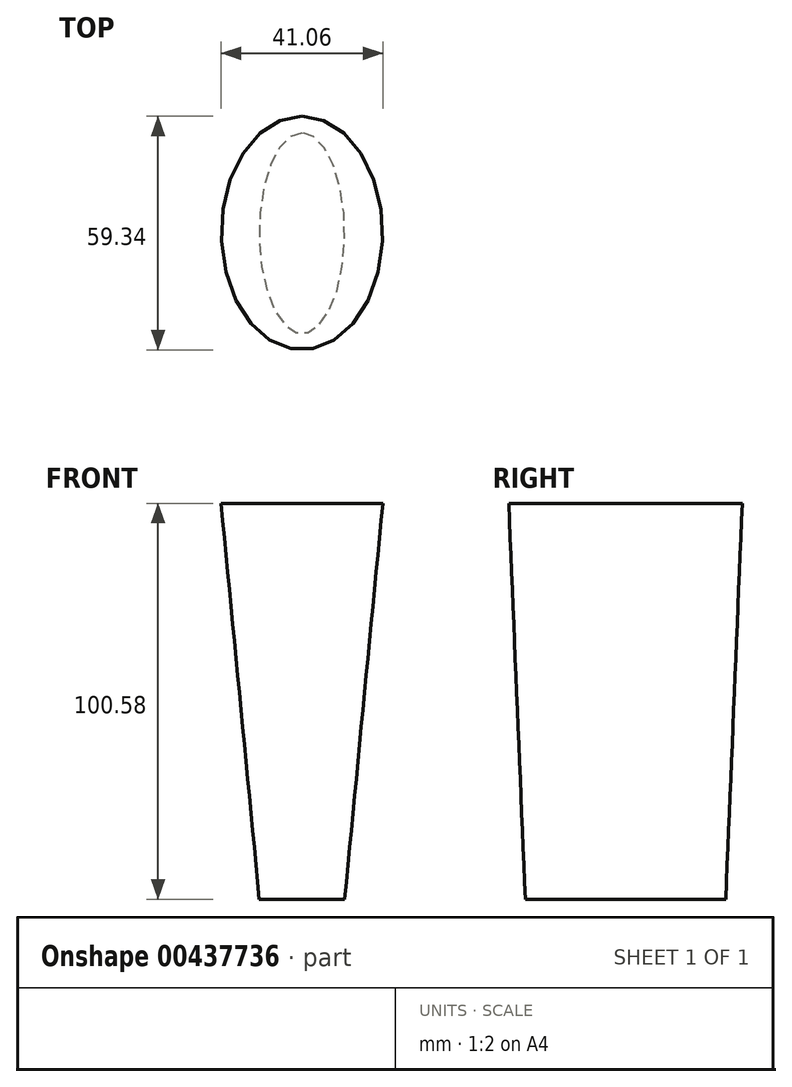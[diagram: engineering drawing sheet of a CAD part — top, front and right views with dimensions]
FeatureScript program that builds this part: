
annotation { "Feature Type Name" : "Feature", "Feature Type Description" : "" }
export const myFeature = defineFeature(function(context is Context, id is Id, definition is map)
    precondition{}
    {
        {
            var Q0;
            Q0=qCreatedBy(makeId("Top.planeOp"),FACE);
            var sketch = newSketch(context, id + "F0", { "sketchPlane" : qUnion([Q0])});
            skEllipse(sketch, "E0", {"center": v(0, 0) * mm, "majorRadius": 25.46 * mm, "minorRadius": 10.85 * mm, "majorAxis": v(0, -1)});
            skPoint(sketch, "E1", {"position": v(0, 25.46) * mm});
            skPoint(sketch, "E2", {"position": v(0, -25.46) * mm});
            skSolve(sketch);
        }
        {
            var Q0;
            Q0=qCreatedBy(makeId("Top.planeOp"),FACE);
            cPlane(context, id + "F1", {"entities" : qUnion([Q0]), "cplaneType" : CPlaneType.OFFSET, "offset" : 100.58 * mm, "width" : 152.4 * mm, "height" : 152.4 * mm});
        }
        {
            var Q0;
            Q0=qCreatedBy(id+"F1.planeOp",FACE);
            var sketch = newSketch(context, id + "F2", { "sketchPlane" : qUnion([Q0])});
            skEllipse(sketch, "E3", {"center": v(0, 0) * mm, "majorRadius": 29.67 * mm, "minorRadius": 20.53 * mm, "majorAxis": v(0, 1)});
            skPoint(sketch, "E4", {"position": v(0, 29.67) * mm});
            skPoint(sketch, "E5", {"position": v(0, -29.67) * mm});
            skSolve(sketch);
        }
        {
            var Q0;
            Q0=makeQuery(id+"F2.imprint","IMPRINT",FACE,{"disambiguationData":[TD([[makeQuery(id+"F2.imprint","IMPRINT",EDGE,{"derivedFrom":sQuery(id+"F2.wireOp",EDGE,"E3")}),1.0]])]});
            var Q1;
            Q1=makeQuery(id+"F0.imprint","IMPRINT",FACE,{"disambiguationData":[TD([[makeQuery(id+"F0.imprint","IMPRINT",EDGE,{"derivedFrom":sQuery(id+"F0.wireOp",EDGE,"E0")}),1.0]])]});
            loft(context, id + "F3", {"sheetProfilesArray" : [{ "sheetProfileEntities" : qUnion([Q0]) }, { "sheetProfileEntities" : qUnion([Q1]) }]});
        }
    });
